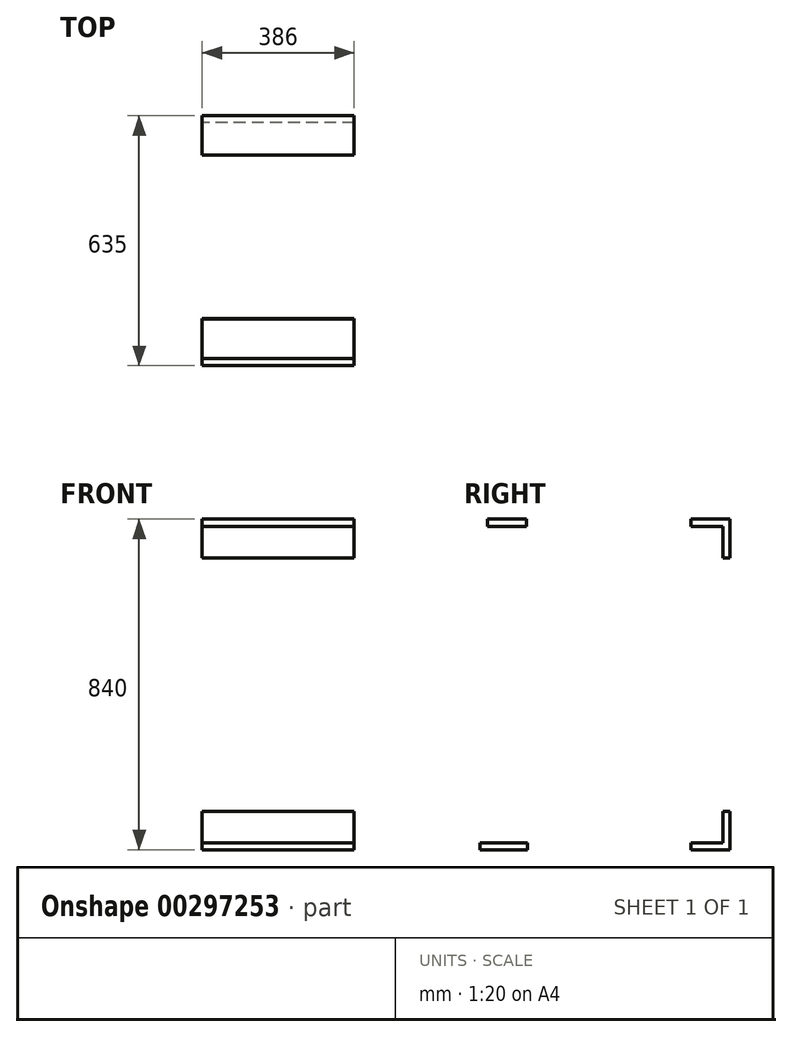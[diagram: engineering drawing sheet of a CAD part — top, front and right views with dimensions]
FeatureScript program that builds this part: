
annotation { "Feature Type Name" : "Feature", "Feature Type Description" : "" }
export const myFeature = defineFeature(function(context is Context, id is Id, definition is map)
    precondition{}
    {
        {
            var Q0;
            Q0=qCreatedBy(makeId("Right.planeOp"),FACE);
            var sketch = newSketch(context, id + "F0", { "sketchPlane" : qUnion([Q0])});
            skLineSegment(sketch, "E0.bottom", {"start": v(317.5, 420) * mm, "end": v(-317.5, 420) * mm, "construction": true});
            skLineSegment(sketch, "E0.top", {"start": v(317.5, -420) * mm, "end": v(-317.5, -420) * mm, "construction": true});
            skLineSegment(sketch, "E0.left", {"start": v(317.5, 420) * mm, "end": v(317.5, -420) * mm, "construction": true});
            skLineSegment(sketch, "E0.right", {"start": v(-317.5, 420) * mm, "end": v(-317.5, -420) * mm, "construction": true});
            skPoint(sketch, "E0.middle", {"position": v(0, 0) * mm});
            skLineSegment(sketch, "E1.bottom", {"start": v(317.5, 420) * mm, "end": v(217.5, 420) * mm});
            skLineSegment(sketch, "E1.top", {"start": v(317.5, 402) * mm, "end": v(217.5, 402) * mm});
            skLineSegment(sketch, "E1.left", {"start": v(317.5, 420) * mm, "end": v(317.5, 402) * mm});
            skLineSegment(sketch, "E1.right", {"start": v(217.5, 420) * mm, "end": v(217.5, 402) * mm});
            skLineSegment(sketch, "E2.bottom", {"start": v(317.5, 402) * mm, "end": v(299.5, 402) * mm});
            skLineSegment(sketch, "E2.top", {"start": v(317.5, 322) * mm, "end": v(299.5, 322) * mm});
            skLineSegment(sketch, "E2.left", {"start": v(317.5, 402) * mm, "end": v(317.5, 322) * mm});
            skLineSegment(sketch, "E2.right", {"start": v(299.5, 402) * mm, "end": v(299.5, 322) * mm});
            skLineSegment(sketch, "E3.bottom", {"start": v(-299.5, 420) * mm, "end": v(-199.5, 420) * mm});
            skLineSegment(sketch, "E3.top", {"start": v(-299.5, 402) * mm, "end": v(-199.5, 402) * mm});
            skLineSegment(sketch, "E3.left", {"start": v(-299.5, 420) * mm, "end": v(-299.5, 402) * mm});
            skLineSegment(sketch, "E3.right", {"start": v(-199.5, 420) * mm, "end": v(-199.5, 402) * mm});
            skLineSegment(sketch, "E4.bottom", {"start": v(-317.5, -420) * mm, "end": v(-197.5, -420) * mm});
            skLineSegment(sketch, "E4.top", {"start": v(-317.5, -402) * mm, "end": v(-197.5, -402) * mm});
            skLineSegment(sketch, "E4.left", {"start": v(-317.5, -420) * mm, "end": v(-317.5, -402) * mm});
            skLineSegment(sketch, "E4.right", {"start": v(-197.5, -420) * mm, "end": v(-197.5, -402) * mm});
            skLineSegment(sketch, "E5.bottom", {"start": v(317.5, -420) * mm, "end": v(217.5, -420) * mm});
            skLineSegment(sketch, "E5.top", {"start": v(317.5, -402) * mm, "end": v(217.5, -402) * mm});
            skLineSegment(sketch, "E5.left", {"start": v(317.5, -420) * mm, "end": v(317.5, -402) * mm});
            skLineSegment(sketch, "E5.right", {"start": v(217.5, -420) * mm, "end": v(217.5, -402) * mm});
            skLineSegment(sketch, "E6.bottom", {"start": v(317.5, -402) * mm, "end": v(299.5, -402) * mm});
            skLineSegment(sketch, "E6.top", {"start": v(317.5, -322) * mm, "end": v(299.5, -322) * mm});
            skLineSegment(sketch, "E6.left", {"start": v(317.5, -402) * mm, "end": v(317.5, -322) * mm});
            skLineSegment(sketch, "E6.right", {"start": v(299.5, -402) * mm, "end": v(299.5, -322) * mm});
            skSolve(sketch);
        }
        {
            var Q0;
            Q0=qSketchRegion(id+"F0",true);
            extrude(context, id + "F1", {"entities" : qUnion([Q0]), "depth" : 386 * mm});
        }
    });
